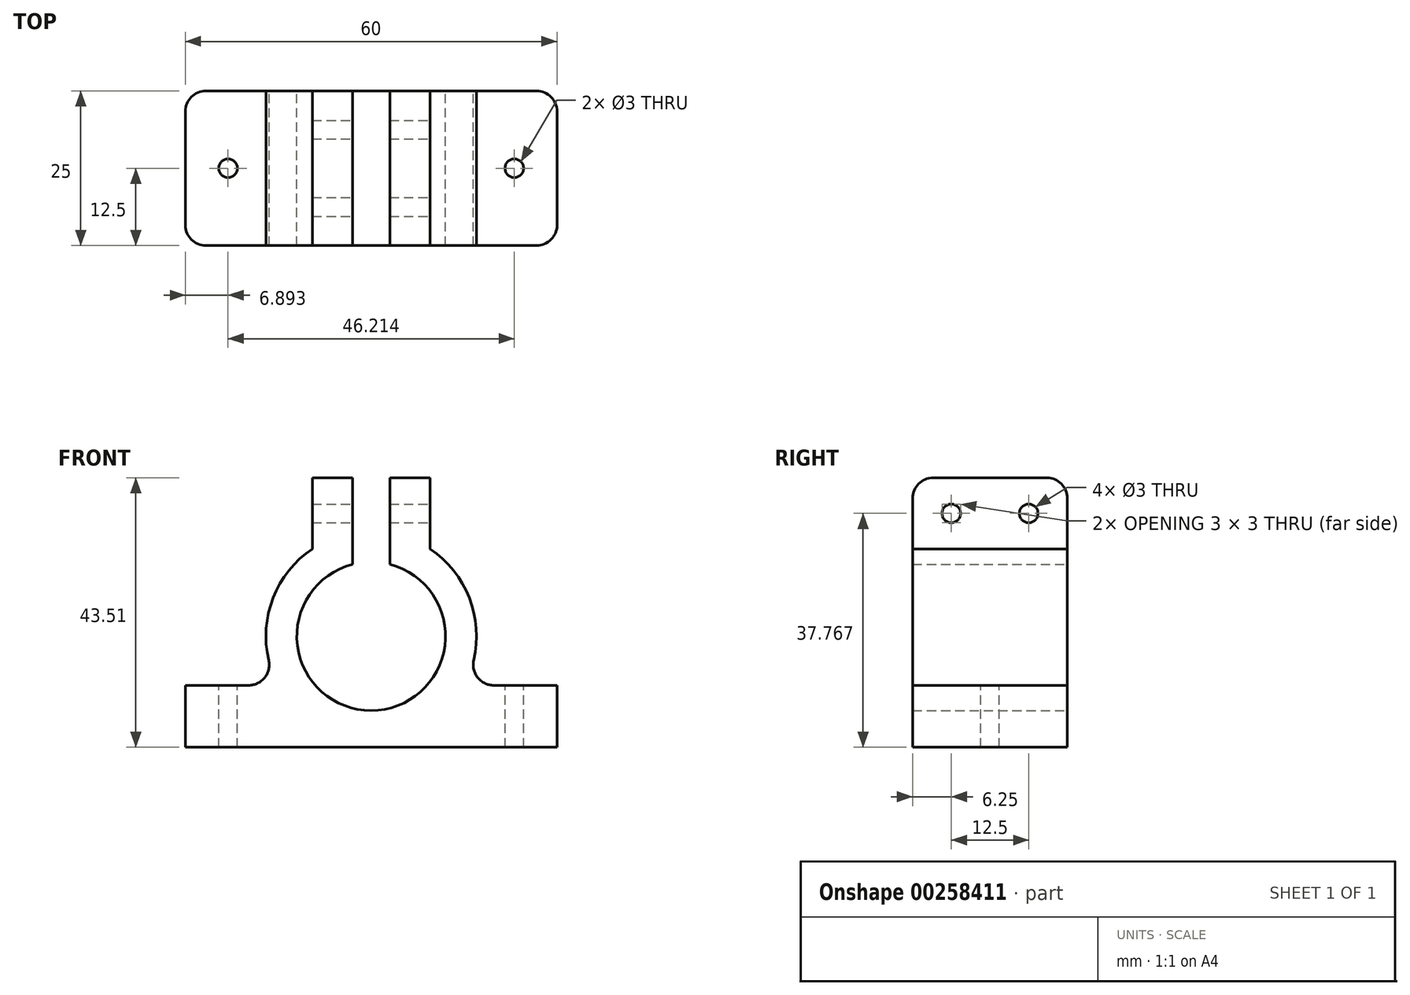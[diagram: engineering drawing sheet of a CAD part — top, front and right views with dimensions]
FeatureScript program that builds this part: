
annotation { "Feature Type Name" : "Feature", "Feature Type Description" : "" }
export const myFeature = defineFeature(function(context is Context, id is Id, definition is map)
    precondition{}
    {
        {
            var Q0;
            Q0=qCreatedBy(makeId("Front.planeOp"),FACE);
            var sketch = newSketch(context, id + "F0", { "sketchPlane" : qUnion([Q0])});
            skLineSegment(sketch, "E0.bottom", {"start": v(30, -29.77) * mm, "end": v(-30, -29.77) * mm});
            skLineSegment(sketch, "E0.left", {"start": v(30, -29.77) * mm, "end": v(30, -19.77) * mm});
            skLineSegment(sketch, "E0.right", {"start": v(-30, -29.77) * mm, "end": v(-30, -19.77) * mm});
            skPoint(sketch, "E0.middle", {"position": v(0, -24.77) * mm});
            skLineSegment(sketch, "E1", {"start": v(0, -29.77) * mm, "end": v(0, 6.08) * mm, "construction": true});
            skArc(sketch, "E2", {"start": v(-3, -0.23) * mm, "mid": v(0, -23.85) * mm, "end": v(3, -0.23) * mm});
            skArc(sketch, "E3.0", {"start": v(15.04, -19.77) * mm, "mid": v(16.49, -7.7) * mm, "end": v(9.5, 2.25) * mm});
            skLineSegment(sketch, "E4", {"start": v(-30, -19.77) * mm, "end": v(-15.04, -19.77) * mm});
            skLineSegment(sketch, "E5.MirrorCS", {"start": v(30, -19.77) * mm, "end": v(15.04, -19.77) * mm});
            skLineSegment(sketch, "E6.top", {"start": v(-9.5, 13.74) * mm, "end": v(-3, 13.74) * mm});
            skLineSegment(sketch, "E6.left", {"start": v(-9.5, 2.25) * mm, "end": v(-9.5, 13.74) * mm});
            skLineSegment(sketch, "E6.right", {"start": v(-3, 4.89) * mm, "end": v(-3, 13.74) * mm});
            skLineSegment(sketch, "E7.MirrorCS", {"start": v(3, 4.89) * mm, "end": v(3, 13.74) * mm});
            skLineSegment(sketch, "E8.MirrorCS", {"start": v(9.5, 2.25) * mm, "end": v(9.5, 13.74) * mm});
            skLineSegment(sketch, "E9.MirrorCS", {"start": v(9.5, 13.74) * mm, "end": v(3, 13.74) * mm});
            skArc(sketch, "E10.trimOffspring", {"start": v(-9.5, 2.25) * mm, "mid": v(-16.49, -7.7) * mm, "end": v(-15.04, -19.77) * mm});
            skPoint(sketch, "E11.orphan", {"position": v(-3, 2.25) * mm});
            skPoint(sketch, "E12.orphan", {"position": v(3, 2.25) * mm});
            skPoint(sketch, "E13.MirrorCS.start.orphan", {"position": v(9.5, 2.25) * mm});
            skLineSegment(sketch, "E14.left", {"start": v(-3, 4.89) * mm, "end": v(-3, -0.23) * mm});
            skLineSegment(sketch, "E14.right", {"start": v(3, 4.89) * mm, "end": v(3, -0.23) * mm});
            skSolve(sketch);
        }
        {
            var Q0;
            Q0=makeQuery(id+"F0.imprint","IMPRINT",FACE,{"disambiguationData":[TD([[makeQuery(id+"F0.imprint","IMPRINT",EDGE,{"derivedFrom":sQuery(id+"F0.wireOp",EDGE,"E0.bottom")}),-1.0]])]});
            extrude(context, id + "F1", {"entities" : qUnion([Q0]), "depth" : 25 * mm});
        }
        {
            var Q0;
            Q0=makeQuery(id+"F1.opExtrude","SWEPT_FACE",FACE,{"disambiguationData":[OSD([sQuery(id+"F0.wireOp",EDGE,"E4")])]});
            var sketch = newSketch(context, id + "F2", { "sketchPlane" : qUnion([Q0])});
            skLineSegment(sketch, "E15", {"start": v(-30, -12.5) * mm, "end": v(30, -12.5) * mm, "construction": true});
            skCircle(sketch, "E16", {"center": v(-23.1, -12.5) * mm, "radius": 1.5 * mm});
            skCircle(sketch, "E17.MirrorC", {"center": v(23.1, -12.5) * mm, "radius": 1.5 * mm});
            skSolve(sketch);
        }
        {
            var Q0;
            Q0 = qSketchRegion(id + "F2", true);
            extrude(context, id + "F3", {"entities" : qUnion([Q0]), "operationType" : NewBodyOperationType.REMOVE, "oppositeDirection" : true, "depth" : 25 * mm});
        }
        {
            var Q0;
            Q0=makeQuery(id+"F1.opExtrude","SWEPT_FACE",FACE,{"disambiguationData":[OSD([sQuery(id+"F0.wireOp",EDGE,"E8.MirrorCS")])]});
            var sketch = newSketch(context, id + "F4", { "sketchPlane" : qUnion([Q0])});
            skLineSegment(sketch, "E18", {"start": v(-25, 8) * mm, "end": v(0, 8) * mm, "construction": true});
            skLineSegment(sketch, "E19", {"start": v(-12.5, 13.74) * mm, "end": v(-12.5, 2.25) * mm, "construction": true});
            skLineSegment(sketch, "E20", {"start": v(-18.75, 13.74) * mm, "end": v(-18.75, 2.25) * mm, "construction": true});
            skLineSegment(sketch, "E21.MirrorCS", {"start": v(-6.25, 13.74) * mm, "end": v(-6.25, 2.25) * mm, "construction": true});
            skCircle(sketch, "E22", {"center": v(-18.75, 8) * mm, "radius": 1.5 * mm});
            skCircle(sketch, "E23", {"center": v(-6.25, 8) * mm, "radius": 1.5 * mm});
            skSolve(sketch);
        }
        {
            var Q0;
            Q0 = qSketchRegion(id + "F4", true);
            extrude(context, id + "F5", {"entities" : qUnion([Q0]), "operationType" : NewBodyOperationType.REMOVE, "oppositeDirection" : true, "depth" : 25 * mm});
        }
        {
            var Q0;
            Q0=makeQuery(id+"F1.opExtrude","CAP_EDGE",EDGE,{"disambiguationData":[OSD([sQuery(id+"F0.wireOp",EDGE,"E6.top")])],"isStart":false});
            var Q1;
            Q1=makeQuery(id+"F1.opExtrude","CAP_EDGE",EDGE,{"disambiguationData":[OSD([sQuery(id+"F0.wireOp",EDGE,"E9.MirrorCS")])],"isStart":false});
            var Q2;
            Q2=makeQuery(id+"F1.opExtrude","CAP_EDGE",EDGE,{"disambiguationData":[OSD([sQuery(id+"F0.wireOp",EDGE,"E6.top")])],"isStart":true});
            var Q3;
            Q3=makeQuery(id+"F1.opExtrude","CAP_EDGE",EDGE,{"disambiguationData":[OSD([sQuery(id+"F0.wireOp",EDGE,"E9.MirrorCS")])],"isStart":true});
            var Q4;
            Q4=makeQuery(id+"F1.opExtrude","CAP_EDGE",EDGE,{"disambiguationData":[OSD([sQuery(id+"F0.wireOp",EDGE,"E0.left")])],"isStart":false});
            var Q5;
            Q5=makeQuery(id+"F1.opExtrude","CAP_EDGE",EDGE,{"disambiguationData":[OSD([sQuery(id+"F0.wireOp",EDGE,"E0.left")])],"isStart":true});
            var Q6;
            Q6=makeQuery(id+"F1.opExtrude","CAP_EDGE",EDGE,{"disambiguationData":[OSD([sQuery(id+"F0.wireOp",EDGE,"E0.right")])],"isStart":true});
            var Q7;
            Q7=makeQuery(id+"F1.opExtrude","CAP_EDGE",EDGE,{"disambiguationData":[OSD([sQuery(id+"F0.wireOp",EDGE,"E0.right")])],"isStart":false});
            var Q8;
            Q8=makeQuery(id+"F1.opExtrude","SWEPT_EDGE",EDGE,{"disambiguationData":[OSD([sQuery(id+"F0.wireOp",EDGE,"E3.0"),sQuery(id+"F0.wireOp",EDGE,"E5.MirrorCS")])]});
            var Q9;
            Q9=makeQuery(id+"F1.opExtrude","SWEPT_EDGE",EDGE,{"disambiguationData":[OSD([sQuery(id+"F0.wireOp",EDGE,"E4"),sQuery(id+"F0.wireOp",EDGE,"E10.trimOffspring")])]});
            fillet(context, id + "F6", {"entities" : qUnion([Q0, Q1, Q2, Q3, Q4, Q5, Q6, Q7, Q8, Q9]), "radius" : 3.31 * mm, "tangentPropagation" : true, "allowEdgeOverflow" : false});
        }
    });
